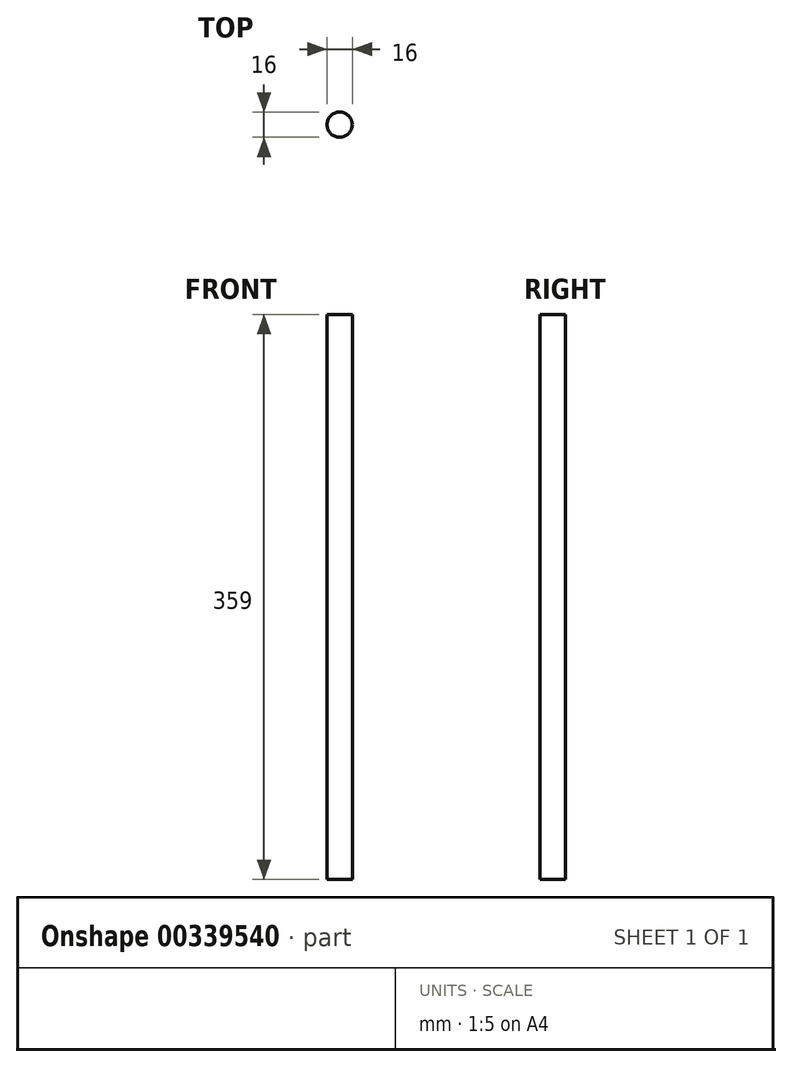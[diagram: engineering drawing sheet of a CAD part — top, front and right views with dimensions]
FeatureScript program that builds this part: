
annotation { "Feature Type Name" : "Feature", "Feature Type Description" : "" }
export const myFeature = defineFeature(function(context is Context, id is Id, definition is map)
    precondition{}
    {
        {
            var Q0;
            Q0=qCreatedBy(makeId("Top.planeOp"),FACE);
            var sketch = newSketch(context, id + "F0", { "sketchPlane" : qUnion([Q0])});
            skCircle(sketch, "E0", {"center": v(-13.8, 5.8) * mm, "radius": 8 * mm});
            skSolve(sketch);
        }
        {
            var Q0;
            Q0=makeQuery(id+"F0.imprint","IMPRINT",FACE,{"disambiguationData":[TD([[makeQuery(id+"F0.imprint","IMPRINT",EDGE,{"derivedFrom":sQuery(id+"F0.wireOp",EDGE,"E0")}),1.0]])]});
            extrude(context, id + "F1", {"entities" : qUnion([Q0]), "depth" : 359 * mm});
        }
    });
